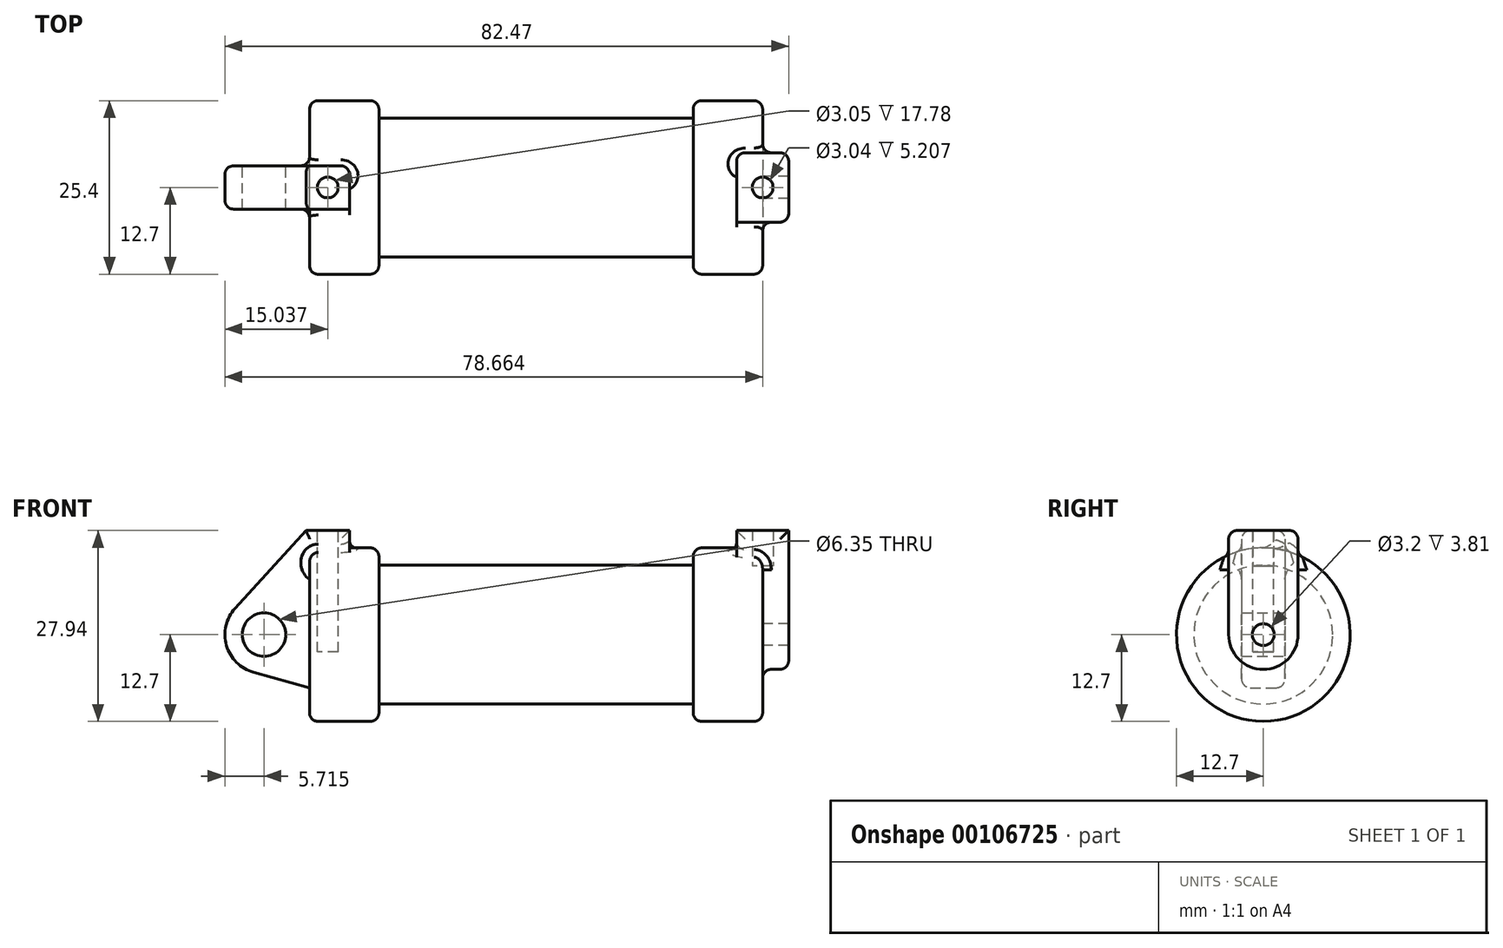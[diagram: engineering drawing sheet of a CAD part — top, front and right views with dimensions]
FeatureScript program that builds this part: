
annotation { "Feature Type Name" : "Feature", "Feature Type Description" : "" }
export const myFeature = defineFeature(function(context is Context, id is Id, definition is map)
    precondition{}
    {
        {
            var Q0;
            Q0=qCreatedBy(makeId("Front.planeOp"),FACE);
            var sketch = newSketch(context, id + "F0", { "sketchPlane" : qUnion([Q0])});
            skLineSegment(sketch, "E0", {"start": v(0, 0) * mm, "end": v(0, 12.7) * mm});
            skLineSegment(sketch, "E1", {"start": v(0, 12.7) * mm, "end": v(10.16, 12.7) * mm});
            skLineSegment(sketch, "E2", {"start": v(10.16, 12.7) * mm, "end": v(10.16, 10.16) * mm});
            skLineSegment(sketch, "E3", {"start": v(10.16, 10.16) * mm, "end": v(56.13, 10.16) * mm});
            skLineSegment(sketch, "E4", {"start": v(56.13, 10.16) * mm, "end": v(56.13, 12.7) * mm});
            skLineSegment(sketch, "E5", {"start": v(56.13, 12.7) * mm, "end": v(66.3, 12.7) * mm});
            skLineSegment(sketch, "E6", {"start": v(66.3, 12.7) * mm, "end": v(66.3, 0) * mm});
            skLineSegment(sketch, "E7", {"start": v(66.3, 0) * mm, "end": v(0, 0) * mm});
            skLineSegment(sketch, "E8", {"start": v(5.84, 15.24) * mm, "end": v(-0.5, 15.24) * mm});
            skLineSegment(sketch, "E9", {"start": v(-0.5, 15.24) * mm, "end": v(-10.88, 3.85) * mm});
            skLineSegment(sketch, "E10", {"start": v(0, 0) * mm, "end": v(-6.65, 0) * mm});
            skCircle(sketch, "E11", {"center": v(-6.65, 0) * mm, "radius": 5.72 * mm});
            skCircle(sketch, "E12", {"center": v(-6.65, 0) * mm, "radius": 3.18 * mm});
            skLineSegment(sketch, "E13", {"start": v(5.84, 15.24) * mm, "end": v(5.84, -9.4) * mm});
            skLineSegment(sketch, "E14", {"start": v(5.84, -9.4) * mm, "end": v(-8.18, -5.5) * mm});
            skSolve(sketch);
        }
        {
            var Q0;
            {var subQ0=sQuery(id+"F0.wireOp",EDGE,"E0");Q0=makeQuery(id+"F0.imprint","IMPRINT",FACE,{"disambiguationData":[TD([[makeQuery(id+"F0.imprint","IMPRINT",EDGE,{"derivedFrom":subQ0}),-1.0]])]});}
            var Q1;
            {var subQ0=sQuery(id+"F0.wireOp",EDGE,"E2");Q1=makeQuery(id+"F0.imprint","IMPRINT",FACE,{"disambiguationData":[TD([[makeQuery(id+"F0.imprint","IMPRINT",EDGE,{"derivedFrom":subQ0}),-1.0]])]});}
            var Q2;
            Q2=sQuery(id+"F0.wireOp",EDGE,"E7");
            revolve(context, id + "F1", {"entities" : qUnion([Q0, Q1]), "axis" : qUnion([Q2]), "revolveType" : RevolveType.FULL});
        }
        {
            var Q0;
            {var subQ3=sQuery(id+"F0.wireOp",EDGE,"E0");Q0=makeQuery(id+"F0.imprint","IMPRINT",FACE,{"disambiguationData":[TD([[makeQuery(id+"F0.imprint","IMPRINT",EDGE,{"derivedFrom":subQ3}),1.0]])]});}
            var Q1;
            {var subQ4=sQuery(id+"F0.wireOp",EDGE,"E12");Q1=makeQuery(id+"F0.imprint","IMPRINT",FACE,{"disambiguationData":[TD([[makeQuery(id+"F0.imprint","IMPRINT",EDGE,{"derivedFrom":subQ4}),-1.0]])]});}
            var Q2;
            {var subQ0=sQuery(id+"F0.wireOp",EDGE,"E14");Q2=makeQuery(id+"F0.imprint","IMPRINT",FACE,{"disambiguationData":[TD([[makeQuery(id+"F0.imprint","IMPRINT",EDGE,{"derivedFrom":subQ0}),-1.0]])]});}
            var Q3;
            {var subQ0=sQuery(id+"F0.wireOp",EDGE,"E0");Q3=makeQuery(id+"F0.imprint","IMPRINT",FACE,{"disambiguationData":[TD([[makeQuery(id+"F0.imprint","IMPRINT",EDGE,{"derivedFrom":subQ0}),-1.0]])]});}
            extrude(context, id + "F2", {"entities" : qUnion([Q0, Q1, Q2, Q3]), "operationType" : NewBodyOperationType.ADD, "endBound" : BoundingType.SYMMETRIC, "depth" : 6.35 * mm});
        }
        {
            var Q0;
            Q0=makeQuery(id+"F1.opRevolve","SWEPT_FACE",FACE,{"disambiguationData":[OSD([sQuery(id+"F0.wireOp",EDGE,"E6")])]});
            var sketch = newSketch(context, id + "F3", { "sketchPlane" : qUnion([Q0])});
            skCircle(sketch, "E15", {"center": v(0, 0) * mm, "radius": 5.08 * mm});
            skCircle(sketch, "E16", {"center": v(0, 0) * mm, "radius": 1.6 * mm});
            skLineSegment(sketch, "E17", {"start": v(5.08, 0) * mm, "end": v(5.08, 15.24) * mm});
            skLineSegment(sketch, "E18", {"start": v(-5.08, 0) * mm, "end": v(-5.08, 15.24) * mm});
            skLineSegment(sketch, "E19", {"start": v(-5.08, 15.24) * mm, "end": v(5.08, 15.24) * mm});
            skSolve(sketch);
        }
        {
            var Q0;
            Q0 = qSketchRegion(id + "F3", true);
            extrude(context, id + "F4", {"entities" : qUnion([Q0]), "operationType" : NewBodyOperationType.ADD, "endBound" : BoundingType.SYMMETRIC, "depth" : 7.62 * mm});
        }
        {
            var Q0;
            Q0=makeQuery(id+"F2.opExtrude","SWEPT_FACE",FACE,{"disambiguationData":[OSD([sQuery(id+"F0.wireOp",EDGE,"E8")])]});
            var sketch = newSketch(context, id + "F5", { "sketchPlane" : qUnion([Q0])});
            skCircle(sketch, "E20", {"center": v(2.67, 0) * mm, "radius": 1.52 * mm});
            skPoint(sketch, "E20.centerSnap0", {"position": v(2.67, -3.18) * mm});
            skSolve(sketch);
        }
        {
            var Q0;
            Q0=makeQuery(id+"F5.imprint","IMPRINT",FACE,{"disambiguationData":[TD([[makeQuery(id+"F5.imprint","IMPRINT",EDGE,{"derivedFrom":sQuery(id+"F5.wireOp",EDGE,"E20")}),1.0]])]});
            var Q1;
            Q1=sQuery(id+"F5.wireOp",EDGE,"E20");
            extrude(context, id + "F6", {"entities" : qUnion([Q0]), "operationType" : NewBodyOperationType.REMOVE, "surfaceEntities" : qUnion([Q1]), "oppositeDirection" : true, "depth" : 17.78 * mm});
        }
        {
            var Q0;
            Q0=makeQuery(id+"F4.opExtrude","SWEPT_FACE",FACE,{"disambiguationData":[OSD([sQuery(id+"F3.wireOp",EDGE,"E19")])]});
            var sketch = newSketch(context, id + "F7", { "sketchPlane" : qUnion([Q0])});
            skPoint(sketch, "E21.centerSnap0", {"position": v(62.48, 0) * mm});
            skCircle(sketch, "E22", {"center": v(66.3, 0) * mm, "radius": 1.52 * mm});
            skPoint(sketch, "E22.centerSnap0", {"position": v(66.3, -5.08) * mm});
            skSolve(sketch);
        }
        {
            var Q0;
            Q0 = qSketchRegion(id + "F7", true);
            extrude(context, id + "F8", {"entities" : qUnion([Q0]), "operationType" : NewBodyOperationType.REMOVE, "endBound" : BoundingType.SYMMETRIC, "depth" : 10.4 * mm});
        }
        {
            var Q0;
            Q0=makeQuery(id+"F4.opExtrude","SWEPT_FACE",FACE,{"disambiguationData":[OSD([sQuery(id+"F3.wireOp",EDGE,"E17")])]});
            var Q1;
            Q1=makeQuery(id+"F4.opExtrude","SWEPT_EDGE",EDGE,{"disambiguationData":[OSD([sQuery(id+"F3.wireOp",EDGE,"E18"),sQuery(id+"F3.wireOp",EDGE,"E19")])]});
            var Q2;
            Q2=makeQuery(id+"F4.boolean.opBoolean","INTERSECT",EDGE,{"derivedFrom":[makeQuery(id+"F1.opRevolve","SWEPT_FACE",FACE,{"disambiguationData":[OSD([sQuery(id+"F0.wireOp",EDGE,"E5")])]}),makeQuery(id+"F4.opExtrude","SWEPT_FACE",FACE,{"disambiguationData":[OSD([sQuery(id+"F3.wireOp",EDGE,"E18")])]})]});
            var Q3;
            Q3=makeQuery(id+"F1.opRevolve","SWEPT_EDGE",EDGE,{"disambiguationData":[OSD([sQuery(id+"F0.wireOp",EDGE,"E4"),sQuery(id+"F0.wireOp",EDGE,"E5")])]});
            var Q4;
            Q4=makeQuery(id+"F1.opRevolve","SWEPT_EDGE",EDGE,{"disambiguationData":[OSD([sQuery(id+"F0.wireOp",EDGE,"E1"),sQuery(id+"F0.wireOp",EDGE,"E2")])]});
            var Q5;
            Q5=makeQuery(id+"F2.opExtrude","CAP_EDGE",EDGE,{"disambiguationData":[OSD([sQuery(id+"F0.wireOp",EDGE,"E13")])],"isStart":true});
            var Q6;
            Q6=makeQuery(id+"F2.opExtrude","CAP_EDGE",EDGE,{"disambiguationData":[OSD([sQuery(id+"F0.wireOp",EDGE,"E8")])],"isStart":true});
            var Q7;
            Q7=makeQuery(id+"F2.boolean.opBoolean","INTERSECT",EDGE,{"derivedFrom":[makeQuery(id+"F1.opRevolve","SWEPT_FACE",FACE,{"disambiguationData":[OSD([sQuery(id+"F0.wireOp",EDGE,"E1")])]}),makeQuery(id+"F2.opExtrude","CAP_FACE",FACE,{"disambiguationData":[OSD([sQuery(id+"F0.wireOp",EDGE,"E8"),sQuery(id+"F0.wireOp",EDGE,"E9"),sQuery(id+"F0.wireOp",EDGE,"E11"),sQuery(id+"F0.wireOp",EDGE,"E12"),sQuery(id+"F0.wireOp",EDGE,"E13"),sQuery(id+"F0.wireOp",EDGE,"E14")])],"isStart":true})]});
            var Q8;
            Q8=makeQuery(id+"F2.opExtrude","CAP_EDGE",EDGE,{"disambiguationData":[OSD([sQuery(id+"F0.wireOp",EDGE,"E8")])],"isStart":false});
            var Q9;
            Q9=makeQuery(id+"F2.boolean.opBoolean","INTERSECT",EDGE,{"derivedFrom":[makeQuery(id+"F1.opRevolve","SWEPT_FACE",FACE,{"disambiguationData":[OSD([sQuery(id+"F0.wireOp",EDGE,"E1")])]}),makeQuery(id+"F2.opExtrude","CAP_FACE",FACE,{"disambiguationData":[OSD([sQuery(id+"F0.wireOp",EDGE,"E8"),sQuery(id+"F0.wireOp",EDGE,"E9"),sQuery(id+"F0.wireOp",EDGE,"E11"),sQuery(id+"F0.wireOp",EDGE,"E12"),sQuery(id+"F0.wireOp",EDGE,"E13"),sQuery(id+"F0.wireOp",EDGE,"E14")])],"isStart":false})]});
            var Q10;
            Q10=makeQuery(id+"F2.opExtrude","CAP_EDGE",EDGE,{"disambiguationData":[OSD([sQuery(id+"F0.wireOp",EDGE,"E9")])],"isStart":false});
            var Q11;
            Q11=makeQuery(id+"F2.opExtrude","CAP_EDGE",EDGE,{"disambiguationData":[OSD([sQuery(id+"F0.wireOp",EDGE,"E11")])],"isStart":true});
            var Q12;
            Q12=makeQuery(id+"F1.opRevolve","SWEPT_EDGE",EDGE,{"disambiguationData":[OSD([sQuery(id+"F0.wireOp",EDGE,"E5"),sQuery(id+"F0.wireOp",EDGE,"E6")])]});
            var Q13;
            Q13=makeQuery(id+"F1.opRevolve","SWEPT_EDGE",EDGE,{"disambiguationData":[OSD([sQuery(id+"F0.wireOp",EDGE,"E0"),sQuery(id+"F0.wireOp",EDGE,"E1")])]});
            fillet(context, id + "F9", {"entities" : qUnion([Q0, Q1, Q2, Q3, Q4, Q5, Q6, Q7, Q8, Q9, Q10, Q11, Q12, Q13]), "radius" : 1.27 * mm, "tangentPropagation" : true, "allowEdgeOverflow" : false});
        }
    });
